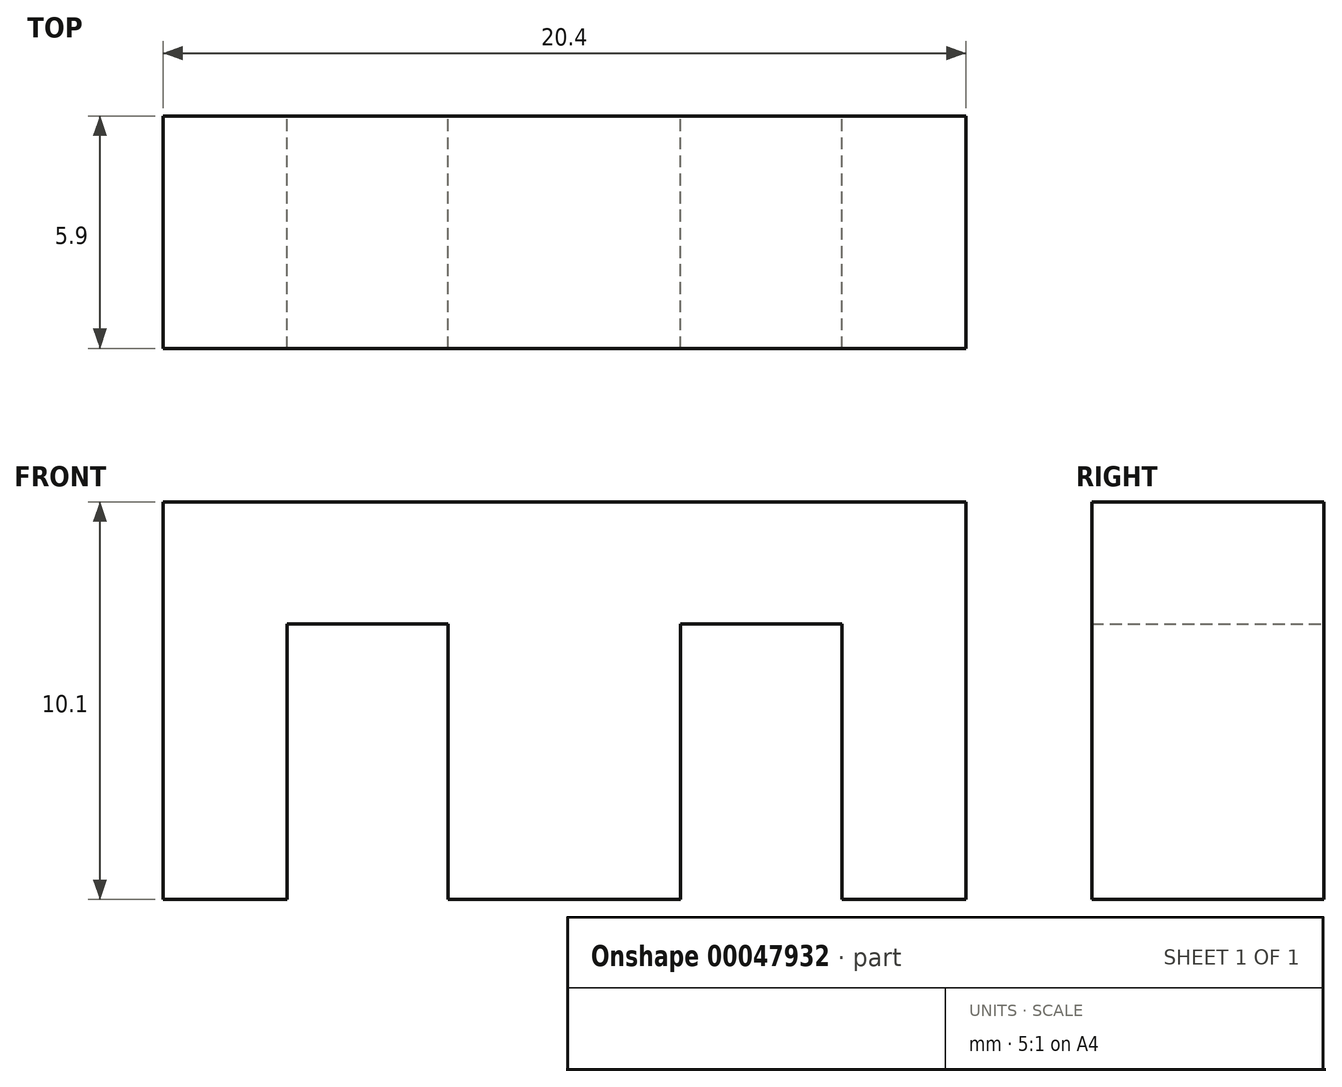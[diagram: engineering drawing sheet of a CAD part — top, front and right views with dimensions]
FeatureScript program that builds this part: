
annotation { "Feature Type Name" : "Feature", "Feature Type Description" : "" }
export const myFeature = defineFeature(function(context is Context, id is Id, definition is map)
    precondition{}
    {
        {
            var Q0;
            Q0=qCreatedBy(makeId("Front.planeOp"),FACE);
            var sketch = newSketch(context, id + "F0", { "sketchPlane" : qUnion([Q0])});
            skLineSegment(sketch, "E0", {"start": v(-10.2, 0) * mm, "end": v(-10.2, 10.1) * mm});
            skLineSegment(sketch, "E1", {"start": v(-10.2, 10.1) * mm, "end": v(10.2, 10.1) * mm});
            skLineSegment(sketch, "E2", {"start": v(10.2, 10.1) * mm, "end": v(10.2, 0) * mm});
            skLineSegment(sketch, "E3", {"start": v(10.2, 0) * mm, "end": v(7.05, 0) * mm});
            skLineSegment(sketch, "E4", {"start": v(7.05, 0) * mm, "end": v(7.05, 7) * mm});
            skLineSegment(sketch, "E5", {"start": v(7.05, 7) * mm, "end": v(2.95, 7) * mm});
            skLineSegment(sketch, "E6", {"start": v(2.95, 7) * mm, "end": v(2.95, 0) * mm});
            skLineSegment(sketch, "E7", {"start": v(2.95, 0) * mm, "end": v(-2.95, 0) * mm});
            skLineSegment(sketch, "E8", {"start": v(-2.95, 0) * mm, "end": v(-2.95, 7) * mm});
            skLineSegment(sketch, "E9", {"start": v(-2.95, 7) * mm, "end": v(-7.05, 7) * mm});
            skLineSegment(sketch, "E10", {"start": v(-7.05, 7) * mm, "end": v(-7.05, 0) * mm});
            skLineSegment(sketch, "E11", {"start": v(-7.05, 0) * mm, "end": v(-10.2, 0) * mm});
            skSolve(sketch);
        }
        {
            var Q0;
            Q0 = qSketchRegion(id + "F0", true);
            extrude(context, id + "F1", {"entities" : qUnion([Q0]), "endBound" : BoundingType.SYMMETRIC, "depth" : 5.9 * mm});
        }
    });
